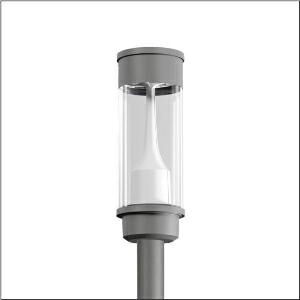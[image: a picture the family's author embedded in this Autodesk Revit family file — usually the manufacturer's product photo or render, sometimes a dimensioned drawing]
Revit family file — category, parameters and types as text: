
# Revit family: litepole_iq___p1_0a_5xa5415ff14h_1a61
name_source: partatom
category: Lighting Fixtures
units: mm (PartAtom-declared; Revit-internal decimal feet)

## family parameters
Cut with Voids When Loaded = No
Host = Face
Light Source = No
Part Type = Normal
Room Calculation Point = No
Round Connector Dimension = Use Diameter
Shared = No

## types (1)
- --- (1 x LED, 1510 lm, 10.5 W, 3000K)
    Apparent Load = 11 VA
    CIE Flux Codes = 32 61 90 93 100
    Color Rendering = 70
    Color Temperature = 3000K
    Default Elevation = 1800 mm
    Description = Litepole iQ, mast luminaire, Module 540 iQ-SR, primary light control with 3 zone facetted reflector, of plastic, silver coated, highly specular, structured, primary optical cover: cover, of PMMA, transparent, light distribution: P1.0a, light emission: direct distribution, primary light characteristic: strongly asymmetric, installation type: post-top, LED, High Power LED, rated luminous flux: 1.510lm, luminous efficacy: 144lm/W, light colour: 730, colour temperature: 3000K, control gear: ECG iQ, control: Auto-Match, Temp-Guard, Lumen-Switch, Night-Set, Smart-Wire, Light-Fading, Desk-Remote (wireless, voltage-free reading and setting of iQ features in the workshop via application-optimized NFC function/RFID function), optimised constant luminous flux control (CLO 2.0), Street-Remote, presetting dimming logarithmic, with terminal, 6-pole, max. 2.5mm², mains connection: 230..240V, AC, 50/60Hz, start of lifetime: 11W, end of service life: 11W, reduction: 5W, luminaire housing, upper part, of glass-fibre reinforced polyester, coated, Siteco® metallic grey (DB 702S), diameter: 210mm, height: 590mm, spigot size: d x l = 76 x 70mm (post-top) | with reducer (optional accessory) 60 x 70mm, post-top mast mounting element, of diecast aluminium, coated, Siteco® metallic grey (DB 702S), Module 540 iQ-SR, traffic white (RAL 9016), equipment: standard, protection rating (complete): IP65, insulation class (complete): insulation class II (safety insulation), certification: CE, ENEC, VDE, packaging unit: 1 piece

Light Distribution: P1.0a
    Height = 590 mm
    Lamp = 1 x LED
    Lamp Light Flux = 1510 lm
    Lamp Power = 10.5 W
    Lamp count = 1
    Length = 220 mm
    Luminous efficacy = 144 lm/W
    Manufacturer = Siteco
    ModVariant = No
    Model = 5XA5415FF14H
    Number of Poles = 1
    OnlyDefault = Yes
    Power Factor = 1
    Product Name = Litepole iQ | P1.0a
    Product group = mast luminaire | pylon top
    ProductGroupID = 6100
    Protection Class = Protection class II
    Protection Degree = IP 65
    RLX_Detail_Level = 1
    RLX_Emergency_Light_Flux = 0 lm
    RLX_Emergency_Type = 0
    RLX_Emergency_Type_DB = No
    RlxData = <blob elided: 63889 chars, md5=361bae05>
    Socket = socket
    Standby Power = 0 W
    System Light Flux = 1510 lm
    System Power = 11 W
    Type Comments = factory setting: luminous flux: 100 % | dim-lin: 254 | 419 mA
    Type Image = l_1006025.jpg
    URL = http://relux.com
    VarID = @adj_091053
    Voltage = 0 V
    Weight = 0.00 kg
    Width = 0 mm  [stored 0 ft]

note: [stored X ft] marks values corroborated as IEEE doubles in the binary element streams (Revit-internal decimal feet)

## geometry (parser evidence)
native form markers: Blend x4, Sweep x13
no freeform markers — native parametric forms only
